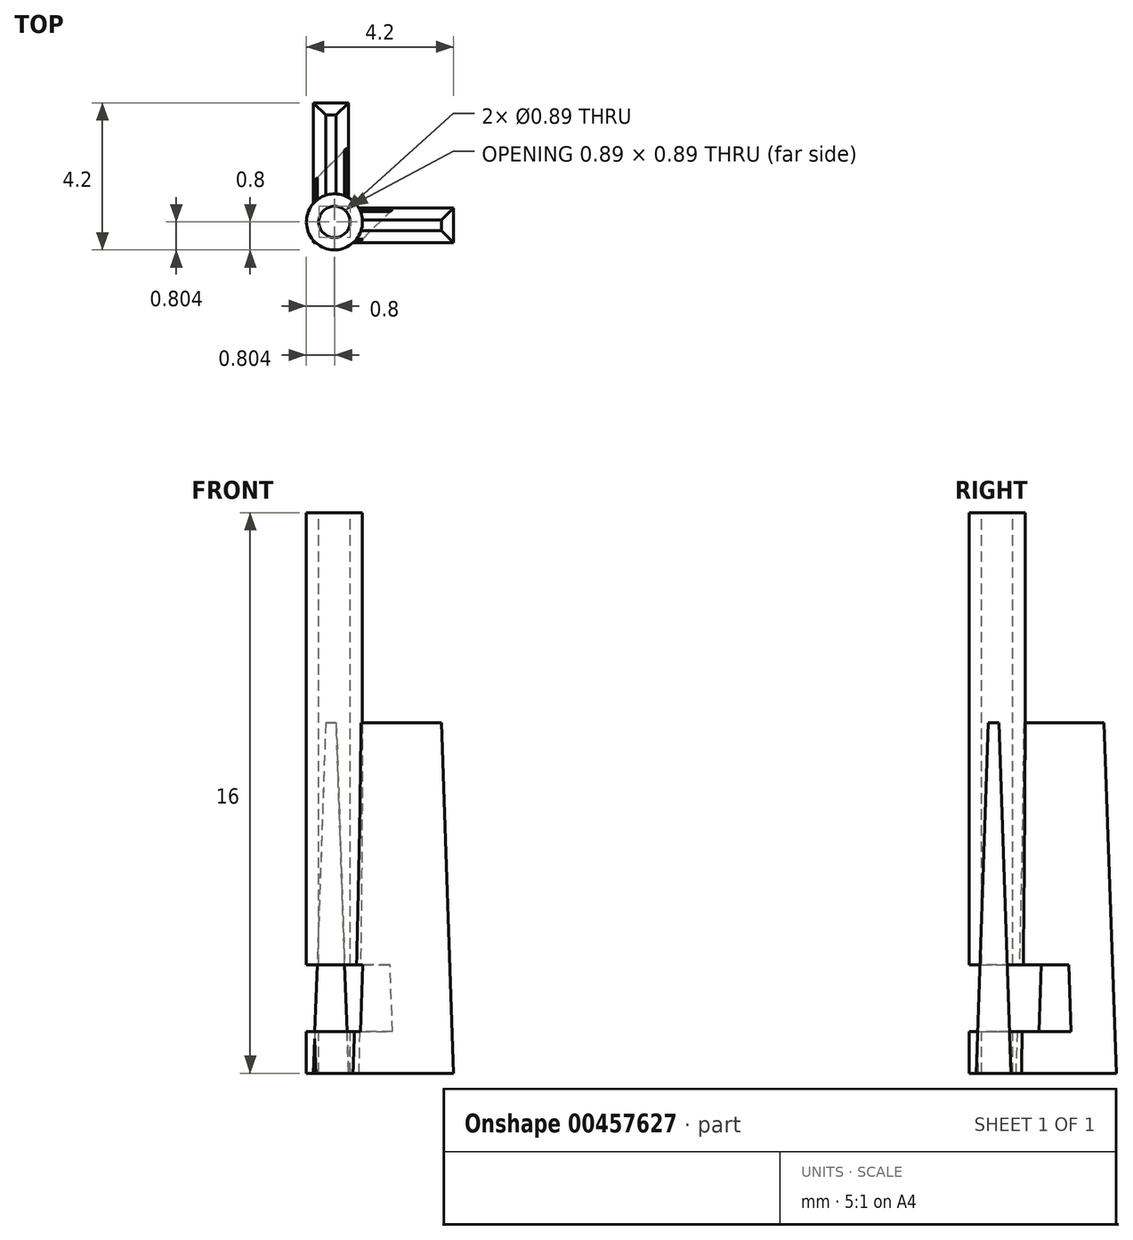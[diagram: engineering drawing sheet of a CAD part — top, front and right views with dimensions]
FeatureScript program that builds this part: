
annotation { "Feature Type Name" : "Feature", "Feature Type Description" : "" }
export const myFeature = defineFeature(function(context is Context, id is Id, definition is map)
    precondition{}
    {
        {
            var Q0;
            Q0=qCreatedBy(makeId("Top.planeOp"),FACE);
            var sketch = newSketch(context, id + "F0", { "sketchPlane" : qUnion([Q0])});
            skLineSegment(sketch, "E0", {"start": v(0, 4) * mm, "end": v(0, 0) * mm});
            skLineSegment(sketch, "E1", {"start": v(0, 0) * mm, "end": v(4, 0) * mm});
            skLineSegment(sketch, "E2", {"start": v(4, 0) * mm, "end": v(4, 1) * mm});
            skLineSegment(sketch, "E3", {"start": v(4, 1) * mm, "end": v(1, 1) * mm});
            skLineSegment(sketch, "E4", {"start": v(1, 1) * mm, "end": v(1, 4) * mm});
            skLineSegment(sketch, "E5", {"start": v(1, 4) * mm, "end": v(0, 4) * mm});
            skSolve(sketch);
        }
        {
            var Q0;
            Q0 = qSketchRegion(id + "F0", true);
            extrude(context, id + "F1", {"entities" : qUnion([Q0]), "depth" : 10 * mm, "offsetDistance" : 25 * mm, "hasDraft" : true, "draftAngle" : 2 * degree, "draftPullDirection" : true});
        }
        {
            var Q0;
            Q0=qCreatedBy(makeId("Top.planeOp"),FACE);
            var sketch = newSketch(context, id + "F2", { "sketchPlane" : qUnion([Q0])});
            skCircle(sketch, "E6", {"center": v(0.6, 0.6) * mm, "radius": 0.8 * mm});
            skSolve(sketch);
        }
        {
            var Q0;
            Q0 = qSketchRegion(id + "F2", true);
            extrude(context, id + "F3", {"entities" : qUnion([Q0]), "operationType" : NewBodyOperationType.ADD, "depth" : 16 * mm, "offsetDistance" : 25 * mm});
        }
        {
            var Q0;
            Q0=makeQuery(id+"F3.opExtrude","CAP_FACE",FACE,{"disambiguationData":[OSD([sQuery(id+"F2.wireOp",EDGE,"E6")])],"isStart":false});
            var sketch = newSketch(context, id + "F4", { "sketchPlane" : qUnion([Q0])});
            skCircle(sketch, "E7", {"center": v(0.6, 0.6) * mm, "radius": 0.45 * mm});
            skSolve(sketch);
        }
        {
            var Q0;
            Q0=makeQuery(id+"F4.imprint","IMPRINT",FACE,{"disambiguationData":[TD([[makeQuery(id+"F4.imprint","IMPRINT",EDGE,{"derivedFrom":sQuery(id+"F4.wireOp",EDGE,"E7")}),1.0]])]});
            extrude(context, id + "F5", {"entities" : qUnion([Q0]), "operationType" : NewBodyOperationType.REMOVE, "endBound" : BoundingType.THROUGH_ALL, "oppositeDirection" : true, "depth" : 25 * mm, "offsetDistance" : 25 * mm});
        }
        {
            var Q0;
            Q0=makeQuery(id+"F1.opExtrude","SWEPT_EDGE",EDGE,{"disambiguationData":[OSD([sQuery(id+"F0.wireOp",EDGE,"E1"),sQuery(id+"F0.wireOp",EDGE,"E2")])]});
            cPlane(context, id + "F6", {"entities" : qUnion([Q0]), "cplaneType" : CPlaneType.LINE_ANGLE, "offset" : 25 * mm, "angle" : 45 * degree, "oppositeDirection" : true, "width" : 150 * mm, "height" : 150 * mm});
        }
        {
            var Q0;
            Q0=qCreatedBy(id+"F6.planeOp",FACE);
            var sketch = newSketch(context, id + "F7", { "sketchPlane" : qUnion([Q0])});
            skLineSegment(sketch, "E8.bottom", {"start": v(0.92, 1.2) * mm, "end": v(-1.24, 1.2) * mm});
            skLineSegment(sketch, "E8.top", {"start": v(0.92, 3.1) * mm, "end": v(-1.24, 3.1) * mm});
            skLineSegment(sketch, "E8.left", {"start": v(0.92, 1.2) * mm, "end": v(0.92, 3.1) * mm});
            skLineSegment(sketch, "E8.right", {"start": v(-1.24, 1.2) * mm, "end": v(-1.24, 3.1) * mm});
            skSolve(sketch);
        }
        {
            var Q0;
            Q0 = qSketchRegion(id + "F7", true);
            extrude(context, id + "F8", {"entities" : qUnion([Q0]), "operationType" : NewBodyOperationType.REMOVE, "depth" : 25 * mm, "offsetDistance" : 25 * mm});
        }
    });
